# Revit family: AF6300
name_source: partatom
category: Generic Models
revit_build: Autodesk Revit MEP 2012 (Build: 20110916_2132(x64)
units: mm (PartAtom-declared; Revit-internal decimal feet)

## types (1)
- AF6300 Unvented Solar Direct (Cylinder)
    15 x 22mm Tundish = Supplied
    3/4" BSP Female x22mm Connection For Expansion vessel = Supplied
    AssetType = Water Heater
    Barcode = 0
    Capacity = 300 Litres
    Control Handle = Yes
    Control Handle Center = Yes
    Controls = Thermostat-adjustable to 65 deg. Expansion relief valve to 6 bar, temperature and pressure relief valve  90 deg. 'C'  and 7 bar, Tundish Pressure reducing valve3 bar, Expansion vessel pre charged to 3bar.
    Electrical Installation connection = To be wired to a suitably rated double pole fused spur.
    Expansion Vessel = Supplied
    Faucet Material = <By Category>
    Finish Options = Corrosion resistant Duplex stainless steel + High performance CFC free injected polyurethane foam insulation.
    Grommet for Solar Sensor = Supplied
    Immersion Heaters = Supplied
    Indirect Heat Exchanger (energy rating) = 22.0kW
    Instruction Manual = Supplied
    Low Emitting Material = Yes
    Manufacturer = Zip Heaters(UK) Ltd
    Mixing Leaver = Yes
    Model = AF6300
    Name = Unvented water heater
    No of Holes = 0
    Percentage of Recycled Content = 0
    Power Rating = 3kW
    SerialNumber = 0
    TagNumber = 0
    Technica support /Maintenance number = 0845 6 005 005 or 0345 6 005 005
    Temperature & Pressure Relief Valve = Supplied
    Tthermostat (High Limit) = Supplied
    Type Comments = Storage water heater.
    Unit Dimensions - W x D x H = 2041mm Height x 545mm Dia.
    Voltage = 230V (50~60Hz)
    Water inlet Connection = 22mm BSP
    Water inlet Pressure Min/Max = Min = 0.15 MPa (1.5 bar) Max = 1.2 MPa (12 bar)
    Website = www.zipheaters.co.uk
    Weight (empty) = 63kg
    Weight (full) = 359kg
    _current revision = 1

## geometry (parser evidence)
native form markers: Sweep x1
no freeform markers — native parametric forms only
